# Revit family: Desk_Screens-Teknion-CQCND_Routes_Infinity_Desk_Edge_Screen-R2018
name_source: partatom
category: Furniture
revit_build: Autodesk Revit 2018 (Build: 20190510_1515(x64)
units: mm (PartAtom-declared; Revit-internal decimal feet)

## family parameters
Always vertical = Yes
Cut with Voids When Loaded = No
OmniClass Number = 23.40.20.00
OmniClass Title = General Furniture and Specialties
Room Calculation Point = No
Shared = Yes
Work Plane-Based = No

## types (4) — shared parameters
Assembly Code = E2020200
Manufacturer = Teknion
Manufacturer Fax = 416.661.4586
Part Number = CQCND
Product Documentation Link = https://assets.teknion.com
Product Line = Routes
Product Page URL = https://www.teknion.com
Series = Routes
Sustainability Data = https://www.teknion.com
URL = www.teknion.com
Unit Weight URL = http://www.teknion.com
Warranty = http://www.teknion.com

## per-type parameters (varying)
| type | Datum Height | Description | Model | Modesty Base Height |
| Partial Modesty Height, 47" Datum Height | 47 " | Routes Infinity Desk Edge Screen, Partial Modesty Height, 47" Datum Height | CQCNDS47__ | 23 " |
| Partial Modesty Height, 42" Datum Height | 42 " | Routes Infinity Desk Edge Screen, Partial Modesty Height, 42" Datum Height | CQCNDS42__ | 23 " |
| Modesty Height, 42" Datum Height | 42 " | Routes Infinity Desk Edge Screen, Modesty Height, 42" Datum Height | CQCNDM42__ | 15 " |
| Modesty Height, 47" Datum Height | 47 " | Routes Infinity Desk Edge Screen, Modesty Height, 47" Datum Height | CQCNDM47__ | 15 " |

## geometry (parser evidence)
native form markers: Sweep x6
no freeform markers — native parametric forms only
